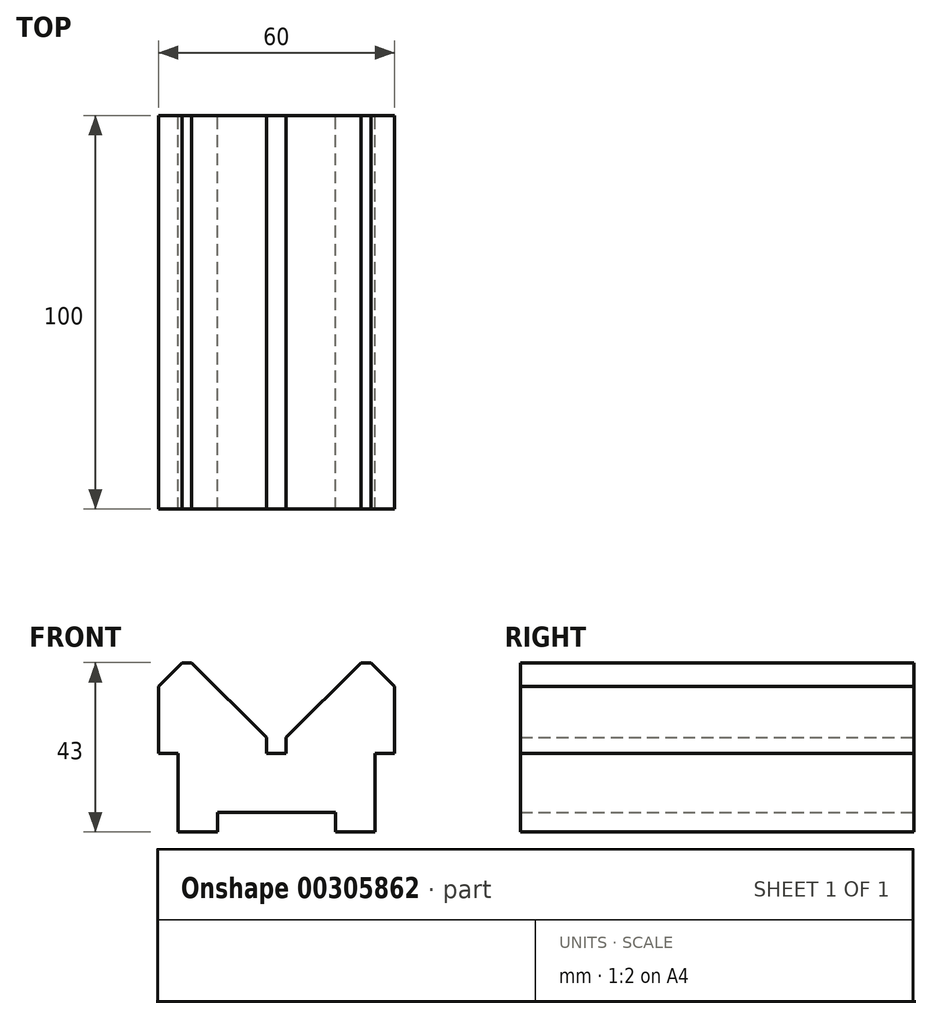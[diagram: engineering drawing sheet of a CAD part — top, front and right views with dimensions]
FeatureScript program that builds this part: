
annotation { "Feature Type Name" : "Feature", "Feature Type Description" : "" }
export const myFeature = defineFeature(function(context is Context, id is Id, definition is map)
    precondition{}
    {
        {
            var Q0;
            Q0=qCreatedBy(makeId("Front.planeOp"),FACE);
            var sketch = newSketch(context, id + "F0", { "sketchPlane" : qUnion([Q0])});
            skLineSegment(sketch, "E0", {"start": v(0, -8.21) * mm, "end": v(-2.5, -8.21) * mm});
            skLineSegment(sketch, "E1", {"start": v(-2.5, -8.21) * mm, "end": v(-2.5, -4.21) * mm});
            skLineSegment(sketch, "E2", {"start": v(-2.5, -4.21) * mm, "end": v(-21.5, 14.79) * mm});
            skLineSegment(sketch, "E3", {"start": v(-21.5, 14.79) * mm, "end": v(-24, 14.79) * mm});
            skLineSegment(sketch, "E4", {"start": v(-24, 14.79) * mm, "end": v(-30, 8.79) * mm});
            skLineSegment(sketch, "E5", {"start": v(-30, 8.79) * mm, "end": v(-30, -8.21) * mm});
            skLineSegment(sketch, "E6", {"start": v(-30, -8.21) * mm, "end": v(-25, -8.21) * mm});
            skLineSegment(sketch, "E7", {"start": v(-25, -8.21) * mm, "end": v(-25, -28.21) * mm});
            skLineSegment(sketch, "E8", {"start": v(-25, -28.21) * mm, "end": v(-15, -28.21) * mm});
            skLineSegment(sketch, "E9", {"start": v(-15, -28.21) * mm, "end": v(-15, -23.21) * mm});
            skLineSegment(sketch, "E10", {"start": v(-15, -23.21) * mm, "end": v(0, -23.21) * mm});
            skLineSegment(sketch, "E11.MirrorCS", {"start": v(0, -8.21) * mm, "end": v(2.5, -8.21) * mm});
            skLineSegment(sketch, "E12.MirrorCS", {"start": v(2.5, -8.21) * mm, "end": v(2.5, -4.21) * mm});
            skLineSegment(sketch, "E13.MirrorCS", {"start": v(2.5, -4.21) * mm, "end": v(21.5, 14.79) * mm});
            skLineSegment(sketch, "E14.MirrorCS", {"start": v(21.5, 14.79) * mm, "end": v(24, 14.79) * mm});
            skLineSegment(sketch, "E15.MirrorCS", {"start": v(24, 14.79) * mm, "end": v(30, 8.79) * mm});
            skLineSegment(sketch, "E16.MirrorCS", {"start": v(30, 8.79) * mm, "end": v(30, -8.21) * mm});
            skLineSegment(sketch, "E17.MirrorCS", {"start": v(30, -8.21) * mm, "end": v(25, -8.21) * mm});
            skLineSegment(sketch, "E18.MirrorCS", {"start": v(25, -8.21) * mm, "end": v(25, -28.21) * mm});
            skLineSegment(sketch, "E19.MirrorCS", {"start": v(25, -28.21) * mm, "end": v(15, -28.21) * mm});
            skLineSegment(sketch, "E20.MirrorCS", {"start": v(15, -28.21) * mm, "end": v(15, -23.21) * mm});
            skLineSegment(sketch, "E21.MirrorCS", {"start": v(15, -23.21) * mm, "end": v(0, -23.21) * mm});
            skSolve(sketch);
        }
        {
            var Q0;
            Q0 = qSketchRegion(id + "F0", true);
            extrude(context, id + "F1", {"entities" : qUnion([Q0]), "endBound" : BoundingType.SYMMETRIC, "depth" : 100 * mm});
        }
    });
